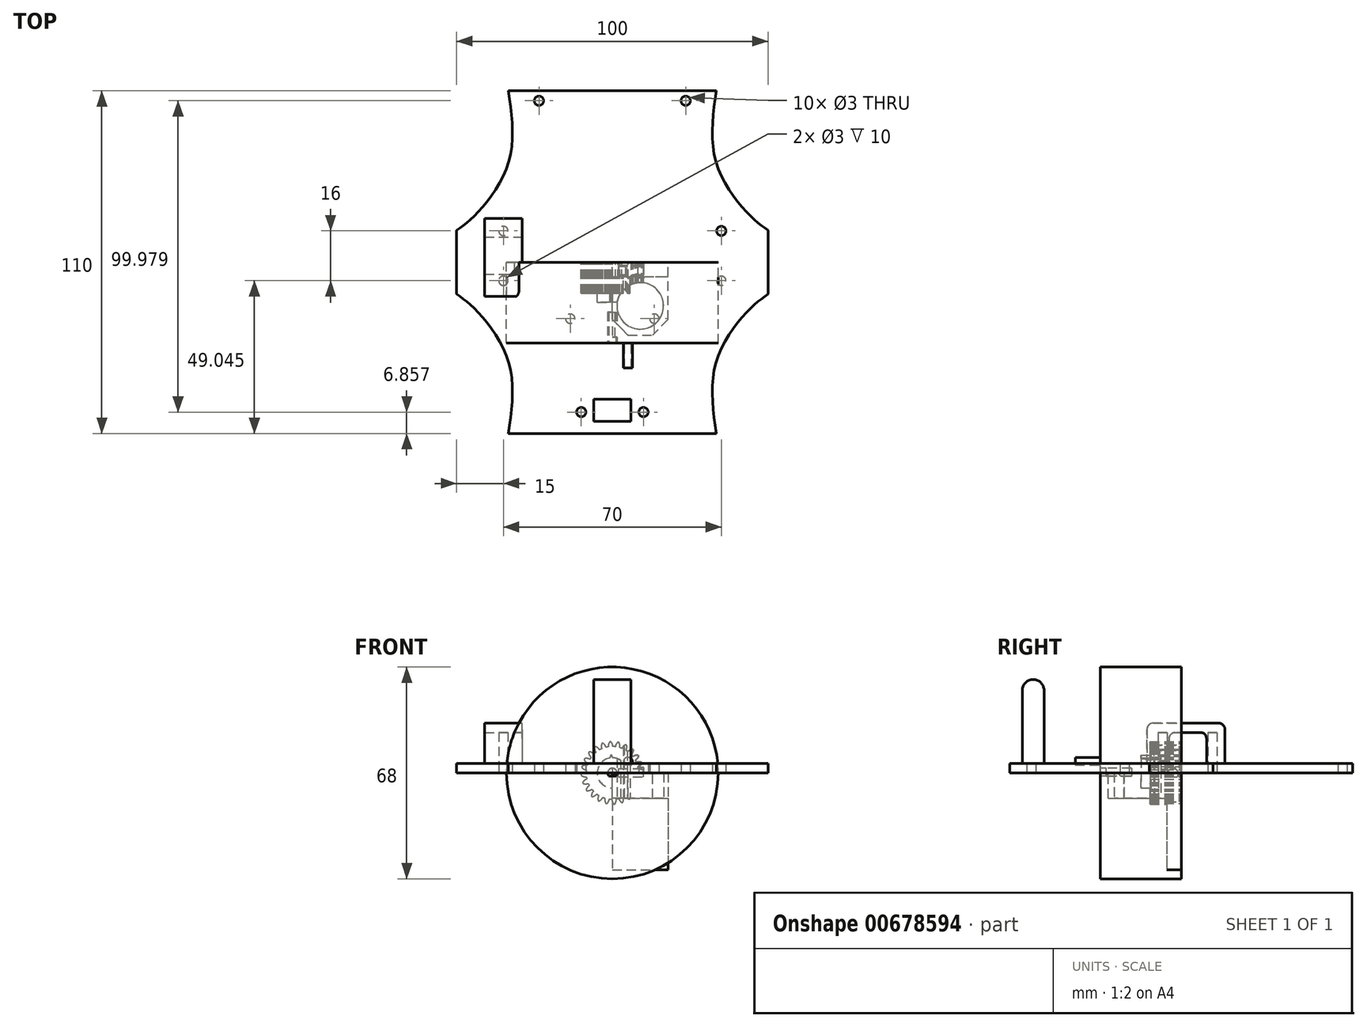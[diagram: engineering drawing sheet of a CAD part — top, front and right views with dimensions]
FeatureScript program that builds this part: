
annotation { "Feature Type Name" : "Feature", "Feature Type Description" : "" }
export const myFeature = defineFeature(function(context is Context, id is Id, definition is map)
    precondition{}
    {
        {
            var Q0;
            Q0=qCreatedBy(makeId("Front.planeOp"),FACE);
            var sketch = newSketch(context, id + "F0", { "sketchPlane" : qUnion([Q0])});
            skCircle(sketch, "E0", {"center": v(0, 0) * mm, "radius": 10 * mm, "construction": true});
            skCircle(sketch, "E1", {"center": v(0, 0) * mm, "radius": 9.24 * mm, "construction": true});
            skCircle(sketch, "E2", {"center": v(0, 0) * mm, "radius": 8.46 * mm});
            skLineSegment(sketch, "E3", {"start": v(0, 0) * mm, "end": v(0, 12.08) * mm, "construction": true});
            skLineSegment(sketch, "E4", {"start": v(0, 0) * mm, "end": v(-0.78, 11.94) * mm, "construction": true});
            skLineSegment(sketch, "E5", {"start": v(0, 9.24) * mm, "end": v(-6.89, 9.24) * mm, "construction": true});
            skLineSegment(sketch, "E6", {"start": v(0, 9.24) * mm, "end": v(-6.45, 6.9) * mm, "construction": true});
            skCircle(sketch, "E7", {"center": v(0, 9.24) * mm, "radius": 2.3 * mm, "construction": true});
            skCircle(sketch, "E8", {"center": v(0, 0) * mm, "radius": 8.68 * mm, "construction": true});
            skArc(sketch, "E9", {"start": v(0.15, 8.46) * mm, "mid": v(-0.02, 9.28) * mm, "end": v(-0.47, 9.99) * mm});
            skArc(sketch, "E10.MirrorCS", {"start": v(-1.26, 8.37) * mm, "mid": v(-1.2, 9.2) * mm, "end": v(-0.84, 9.97) * mm});
            skArc(sketch, "E11", {"start": v(-0.47, 9.99) * mm, "mid": v(-0.65, 9.99) * mm, "end": v(-0.84, 9.97) * mm});
            skArc(sketch, "E12.1.0", {"start": v(-2.04, 8.21) * mm, "mid": v(-2.42, 8.96) * mm, "end": v(-3.04, 9.53) * mm});
            skArc(sketch, "E12.1.1", {"start": v(-3.38, 7.76) * mm, "mid": v(-3.54, 8.58) * mm, "end": v(-3.39, 9.4) * mm});
            skArc(sketch, "E12.1.2", {"start": v(-3.04, 9.53) * mm, "mid": v(-3.22, 9.48) * mm, "end": v(-3.39, 9.4) * mm});
            skArc(sketch, "E12.2.0", {"start": v(-4.1, 7.4) * mm, "mid": v(-4.66, 8.03) * mm, "end": v(-5.4, 8.41) * mm});
            skArc(sketch, "E12.2.1", {"start": v(-5.27, 6.62) * mm, "mid": v(-5.64, 7.37) * mm, "end": v(-5.7, 8.21) * mm});
            skArc(sketch, "E12.2.2", {"start": v(-5.4, 8.41) * mm, "mid": v(-5.56, 8.32) * mm, "end": v(-5.7, 8.21) * mm});
            skArc(sketch, "E12.3.0", {"start": v(-5.87, 6.1) * mm, "mid": v(-6.58, 6.55) * mm, "end": v(-7.4, 6.73) * mm});
            skArc(sketch, "E12.3.1", {"start": v(-6.8, 5.03) * mm, "mid": v(-7.35, 5.66) * mm, "end": v(-7.64, 6.46) * mm});
            skArc(sketch, "E12.3.2", {"start": v(-7.4, 6.73) * mm, "mid": v(-7.53, 6.6) * mm, "end": v(-7.64, 6.46) * mm});
            skArc(sketch, "E12.4.0", {"start": v(-7.25, 4.36) * mm, "mid": v(-8.05, 4.63) * mm, "end": v(-8.89, 4.58) * mm});
            skArc(sketch, "E12.4.1", {"start": v(-7.87, 3.1) * mm, "mid": v(-8.57, 3.57) * mm, "end": v(-9.05, 4.26) * mm});
            skArc(sketch, "E12.4.2", {"start": v(-8.89, 4.58) * mm, "mid": v(-8.98, 4.43) * mm, "end": v(-9.05, 4.26) * mm});
            skArc(sketch, "E12.5.0", {"start": v(-8.13, 2.34) * mm, "mid": v(-8.97, 2.39) * mm, "end": v(-9.77, 2.13) * mm});
            skArc(sketch, "E12.5.1", {"start": v(-8.4, 0.95) * mm, "mid": v(-9.2, 1.23) * mm, "end": v(-9.84, 1.77) * mm});
            skArc(sketch, "E12.5.2", {"start": v(-9.77, 2.13) * mm, "mid": v(-9.82, 1.95) * mm, "end": v(-9.84, 1.77) * mm});
            skArc(sketch, "E12.6.0", {"start": v(-8.46, 0.15) * mm, "mid": v(-9.28, -0.02) * mm, "end": v(-9.99, -0.47) * mm});
            skArc(sketch, "E12.6.1", {"start": v(-8.37, -1.26) * mm, "mid": v(-9.2, -1.2) * mm, "end": v(-9.97, -0.84) * mm});
            skArc(sketch, "E12.6.2", {"start": v(-9.99, -0.47) * mm, "mid": v(-9.99, -0.65) * mm, "end": v(-9.97, -0.84) * mm});
            skArc(sketch, "E12.7.0", {"start": v(-8.21, -2.04) * mm, "mid": v(-8.96, -2.42) * mm, "end": v(-9.53, -3.04) * mm});
            skArc(sketch, "E12.7.1", {"start": v(-7.76, -3.38) * mm, "mid": v(-8.58, -3.54) * mm, "end": v(-9.4, -3.39) * mm});
            skArc(sketch, "E12.7.2", {"start": v(-9.53, -3.04) * mm, "mid": v(-9.48, -3.22) * mm, "end": v(-9.4, -3.39) * mm});
            skArc(sketch, "E12.8.0", {"start": v(-7.4, -4.1) * mm, "mid": v(-8.03, -4.66) * mm, "end": v(-8.41, -5.4) * mm});
            skArc(sketch, "E12.8.1", {"start": v(-6.62, -5.27) * mm, "mid": v(-7.37, -5.64) * mm, "end": v(-8.21, -5.7) * mm});
            skArc(sketch, "E12.8.2", {"start": v(-8.41, -5.4) * mm, "mid": v(-8.32, -5.56) * mm, "end": v(-8.21, -5.7) * mm});
            skArc(sketch, "E12.9.0", {"start": v(-6.1, -5.87) * mm, "mid": v(-6.55, -6.58) * mm, "end": v(-6.73, -7.4) * mm});
            skArc(sketch, "E12.9.1", {"start": v(-5.03, -6.8) * mm, "mid": v(-5.66, -7.35) * mm, "end": v(-6.46, -7.64) * mm});
            skArc(sketch, "E12.9.2", {"start": v(-6.73, -7.4) * mm, "mid": v(-6.6, -7.53) * mm, "end": v(-6.46, -7.64) * mm});
            skArc(sketch, "E12.10.0", {"start": v(-4.36, -7.25) * mm, "mid": v(-4.63, -8.05) * mm, "end": v(-4.58, -8.89) * mm});
            skArc(sketch, "E12.10.1", {"start": v(-3.1, -7.87) * mm, "mid": v(-3.57, -8.57) * mm, "end": v(-4.26, -9.05) * mm});
            skArc(sketch, "E12.10.2", {"start": v(-4.58, -8.89) * mm, "mid": v(-4.43, -8.98) * mm, "end": v(-4.26, -9.05) * mm});
            skArc(sketch, "E12.11.0", {"start": v(-2.34, -8.13) * mm, "mid": v(-2.39, -8.97) * mm, "end": v(-2.13, -9.77) * mm});
            skArc(sketch, "E12.11.1", {"start": v(-0.95, -8.4) * mm, "mid": v(-1.23, -9.2) * mm, "end": v(-1.77, -9.84) * mm});
            skArc(sketch, "E12.11.2", {"start": v(-2.13, -9.77) * mm, "mid": v(-1.95, -9.82) * mm, "end": v(-1.77, -9.84) * mm});
            skArc(sketch, "E12.12.0", {"start": v(-0.15, -8.46) * mm, "mid": v(0.02, -9.28) * mm, "end": v(0.47, -9.99) * mm});
            skArc(sketch, "E12.12.1", {"start": v(1.26, -8.37) * mm, "mid": v(1.2, -9.2) * mm, "end": v(0.84, -9.97) * mm});
            skArc(sketch, "E12.12.2", {"start": v(0.47, -9.99) * mm, "mid": v(0.65, -9.99) * mm, "end": v(0.84, -9.97) * mm});
            skArc(sketch, "E12.13.0", {"start": v(2.04, -8.21) * mm, "mid": v(2.42, -8.96) * mm, "end": v(3.04, -9.53) * mm});
            skArc(sketch, "E12.13.1", {"start": v(3.38, -7.76) * mm, "mid": v(3.54, -8.58) * mm, "end": v(3.39, -9.4) * mm});
            skArc(sketch, "E12.13.2", {"start": v(3.04, -9.53) * mm, "mid": v(3.22, -9.48) * mm, "end": v(3.39, -9.4) * mm});
            skArc(sketch, "E12.14.0", {"start": v(4.1, -7.4) * mm, "mid": v(4.66, -8.03) * mm, "end": v(5.4, -8.41) * mm});
            skArc(sketch, "E12.14.1", {"start": v(5.27, -6.62) * mm, "mid": v(5.64, -7.37) * mm, "end": v(5.7, -8.21) * mm});
            skArc(sketch, "E12.14.2", {"start": v(5.4, -8.41) * mm, "mid": v(5.56, -8.32) * mm, "end": v(5.7, -8.21) * mm});
            skArc(sketch, "E12.15.0", {"start": v(5.87, -6.1) * mm, "mid": v(6.58, -6.55) * mm, "end": v(7.4, -6.73) * mm});
            skArc(sketch, "E12.15.1", {"start": v(6.8, -5.03) * mm, "mid": v(7.35, -5.66) * mm, "end": v(7.64, -6.46) * mm});
            skArc(sketch, "E12.15.2", {"start": v(7.4, -6.73) * mm, "mid": v(7.53, -6.6) * mm, "end": v(7.64, -6.46) * mm});
            skArc(sketch, "E12.16.0", {"start": v(7.25, -4.36) * mm, "mid": v(8.05, -4.63) * mm, "end": v(8.89, -4.58) * mm});
            skArc(sketch, "E12.16.1", {"start": v(7.87, -3.1) * mm, "mid": v(8.57, -3.57) * mm, "end": v(9.05, -4.26) * mm});
            skArc(sketch, "E12.16.2", {"start": v(8.89, -4.58) * mm, "mid": v(8.98, -4.43) * mm, "end": v(9.05, -4.26) * mm});
            skArc(sketch, "E12.17.0", {"start": v(8.13, -2.34) * mm, "mid": v(8.97, -2.39) * mm, "end": v(9.77, -2.13) * mm});
            skArc(sketch, "E12.17.1", {"start": v(8.4, -0.95) * mm, "mid": v(9.2, -1.23) * mm, "end": v(9.84, -1.77) * mm});
            skArc(sketch, "E12.17.2", {"start": v(9.77, -2.13) * mm, "mid": v(9.82, -1.95) * mm, "end": v(9.84, -1.77) * mm});
            skArc(sketch, "E12.18.0", {"start": v(8.46, -0.15) * mm, "mid": v(9.28, 0.02) * mm, "end": v(9.99, 0.47) * mm});
            skArc(sketch, "E12.18.1", {"start": v(8.37, 1.26) * mm, "mid": v(9.2, 1.2) * mm, "end": v(9.97, 0.84) * mm});
            skArc(sketch, "E12.18.2", {"start": v(9.99, 0.47) * mm, "mid": v(9.99, 0.65) * mm, "end": v(9.97, 0.84) * mm});
            skArc(sketch, "E12.19.0", {"start": v(8.21, 2.04) * mm, "mid": v(8.96, 2.42) * mm, "end": v(9.53, 3.04) * mm});
            skArc(sketch, "E12.19.1", {"start": v(7.76, 3.38) * mm, "mid": v(8.58, 3.54) * mm, "end": v(9.4, 3.39) * mm});
            skArc(sketch, "E12.19.2", {"start": v(9.53, 3.04) * mm, "mid": v(9.48, 3.22) * mm, "end": v(9.4, 3.39) * mm});
            skArc(sketch, "E12.20.0", {"start": v(7.4, 4.1) * mm, "mid": v(8.03, 4.66) * mm, "end": v(8.41, 5.4) * mm});
            skArc(sketch, "E12.20.1", {"start": v(6.62, 5.27) * mm, "mid": v(7.37, 5.64) * mm, "end": v(8.21, 5.7) * mm});
            skArc(sketch, "E12.20.2", {"start": v(8.41, 5.4) * mm, "mid": v(8.32, 5.56) * mm, "end": v(8.21, 5.7) * mm});
            skArc(sketch, "E12.21.0", {"start": v(6.1, 5.87) * mm, "mid": v(6.55, 6.58) * mm, "end": v(6.73, 7.4) * mm});
            skArc(sketch, "E12.21.1", {"start": v(5.03, 6.8) * mm, "mid": v(5.66, 7.35) * mm, "end": v(6.46, 7.64) * mm});
            skArc(sketch, "E12.21.2", {"start": v(6.73, 7.4) * mm, "mid": v(6.6, 7.53) * mm, "end": v(6.46, 7.64) * mm});
            skArc(sketch, "E12.22.0", {"start": v(4.36, 7.25) * mm, "mid": v(4.63, 8.05) * mm, "end": v(4.58, 8.89) * mm});
            skArc(sketch, "E12.22.1", {"start": v(3.1, 7.87) * mm, "mid": v(3.57, 8.57) * mm, "end": v(4.26, 9.05) * mm});
            skArc(sketch, "E12.22.2", {"start": v(4.58, 8.89) * mm, "mid": v(4.43, 8.98) * mm, "end": v(4.26, 9.05) * mm});
            skArc(sketch, "E12.23.0", {"start": v(2.34, 8.13) * mm, "mid": v(2.39, 8.97) * mm, "end": v(2.13, 9.77) * mm});
            skArc(sketch, "E12.23.1", {"start": v(0.95, 8.4) * mm, "mid": v(1.23, 9.2) * mm, "end": v(1.77, 9.84) * mm});
            skArc(sketch, "E12.23.2", {"start": v(2.13, 9.77) * mm, "mid": v(1.95, 9.82) * mm, "end": v(1.77, 9.84) * mm});
            skCircle(sketch, "E13", {"center": v(-3.42, 7.98) * mm, "radius": 3.64 * mm, "construction": true});
            skSolve(sketch);
        }
        {
            var Q0;
            Q0=qSketchRegion(id+"F0",true);
            extrude(context, id + "F1", {"entities" : qUnion([Q0]), "depth" : 10 * mm});
        }
        {
            var Q0;
            Q0=qCreatedBy(makeId("Front.planeOp"),FACE);
            var sketch = newSketch(context, id + "F2", { "sketchPlane" : qUnion([Q0])});
            skCircle(sketch, "E14", {"center": v(0, 0) * mm, "radius": 2.31 * mm, "construction": true});
            skCircle(sketch, "E15", {"center": v(0, 0) * mm, "radius": 2.12 * mm});
            skCircle(sketch, "E16", {"center": v(0, 0) * mm, "radius": 2.5 * mm, "construction": true});
            skLineSegment(sketch, "E17", {"start": v(0, 0) * mm, "end": v(0, 3.7) * mm, "construction": true});
            skLineSegment(sketch, "E18", {"start": v(0, 0) * mm, "end": v(-0.23, 3.58) * mm, "construction": true});
            skLineSegment(sketch, "E19", {"start": v(0, 2.31) * mm, "end": v(-2.42, 1.43) * mm, "construction": true});
            skLineSegment(sketch, "E20", {"start": v(0, 2.3) * mm, "end": v(-1.97, 2.3) * mm, "construction": true});
            skCircle(sketch, "E21", {"center": v(0, 0) * mm, "radius": 2.17 * mm, "construction": true});
            skCircle(sketch, "E22", {"center": v(-0.54, 2.1) * mm, "radius": 0.57 * mm, "construction": true});
            skArc(sketch, "E23", {"start": v(0.04, 2.11) * mm, "mid": v(0.03, 2.21) * mm, "end": v(0, 2.31) * mm});
            skArc(sketch, "E24", {"start": v(0, 2.3) * mm, "mid": v(-0.05, 2.4) * mm, "end": v(-0.12, 2.5) * mm});
            skArc(sketch, "E25.MirrorCS", {"start": v(-0.3, 2.3) * mm, "mid": v(-0.27, 2.4) * mm, "end": v(-0.21, 2.5) * mm});
            skArc(sketch, "E26.MirrorCS", {"start": v(-0.32, 2.1) * mm, "mid": v(-0.32, 2.2) * mm, "end": v(-0.3, 2.3) * mm});
            skArc(sketch, "E27", {"start": v(-0.12, 2.5) * mm, "mid": v(-0.16, 2.5) * mm, "end": v(-0.21, 2.5) * mm});
            skArc(sketch, "E28.1.0", {"start": v(-1.83, -1.4) * mm, "mid": v(-1.94, -1.43) * mm, "end": v(-2.05, -1.43) * mm});
            skArc(sketch, "E28.1.1", {"start": v(-1.65, -1.32) * mm, "mid": v(-1.74, -1.37) * mm, "end": v(-1.83, -1.4) * mm});
            skArc(sketch, "E28.1.2", {"start": v(-2.1, -1.35) * mm, "mid": v(-2.08, -1.4) * mm, "end": v(-2.05, -1.43) * mm});
            skArc(sketch, "E28.2.0", {"start": v(2.13, -0.88) * mm, "mid": v(2.2, -0.97) * mm, "end": v(2.26, -1.06) * mm});
            skArc(sketch, "E28.2.1", {"start": v(1.97, -0.77) * mm, "mid": v(2.06, -0.82) * mm, "end": v(2.13, -0.88) * mm});
            skArc(sketch, "E28.2.2", {"start": v(2.22, -1.15) * mm, "mid": v(2.25, -1.1) * mm, "end": v(2.26, -1.06) * mm});
            skCircle(sketch, "E29", {"center": v(0, 2.31) * mm, "radius": 0.57 * mm, "construction": true});
            skSolve(sketch);
        }
        {
            var Q0;
            Q0=qSketchRegion(id+"F2",true);
            extrude(context, id + "F3", {"entities" : qUnion([Q0]), "depth" : 5.62 * mm});
        }
        {
            var Q0;
            Q0=makeQuery(id+"F3.opExtrude","SWEPT_BODY",BODY,{"disambiguationData":[OSD([sQuery(id+"F2.wireOp",EDGE,"E15"),sQuery(id+"F2.wireOp",EDGE,"E23"),sQuery(id+"F2.wireOp",EDGE,"E24"),sQuery(id+"F2.wireOp",EDGE,"E25.MirrorCS"),sQuery(id+"F2.wireOp",EDGE,"E26.MirrorCS"),sQuery(id+"F2.wireOp",EDGE,"E27")])]});
            var Q1;
            Q1=qCreatedBy(makeId("Origin.pointOp"),VERTEX);
            transform(context, id + "F4", {"entities" : qUnion([Q0]), "transformType" : TransformType.SCALE_UNIFORMLY, "scale" : 2.3, "scalePoint" : qUnion([Q1]), "makeCopy" : false});
        }
        {
            var Q0;
            Q0=qCreatedBy(makeId("Front.planeOp"),FACE);
            var sketch = newSketch(context, id + "F5", { "sketchPlane" : qUnion([Q0])});
            skLineSegment(sketch, "E30.bottom", {"start": v(0, 0) * mm, "end": v(17.91, 0) * mm});
            skLineSegment(sketch, "E30.top", {"start": v(0, -31.13) * mm, "end": v(17.91, -31.13) * mm});
            skLineSegment(sketch, "E30.left", {"start": v(0, 0) * mm, "end": v(0, -31.13) * mm});
            skLineSegment(sketch, "E30.right", {"start": v(17.91, 0) * mm, "end": v(17.91, -31.13) * mm});
            skSolve(sketch);
        }
        {
            var Q0;
            Q0=qSketchRegion(id+"F5",true);
            extrude(context, id + "F6", {"entities" : qUnion([Q0]), "depth" : 4.6 * mm, "offsetDistance" : 25 * mm});
        }
        {
            var Q0;
            Q0=makeQuery(id+"F6.opExtrude","CAP_FACE",FACE,{"disambiguationData":[OSD([sQuery(id+"F5.wireOp",EDGE,"E30.bottom"),sQuery(id+"F5.wireOp",EDGE,"E30.top"),sQuery(id+"F5.wireOp",EDGE,"E30.left"),sQuery(id+"F5.wireOp",EDGE,"E30.right")])],"isStart":false});
            var sketch = newSketch(context, id + "F7", { "sketchPlane" : qUnion([Q0])});
            skLineSegment(sketch, "E31.bottom", {"start": v(0, 0) * mm, "end": v(17.91, 0) * mm});
            skLineSegment(sketch, "E31.top", {"start": v(0, -8.15) * mm, "end": v(17.91, -8.15) * mm});
            skLineSegment(sketch, "E31.left", {"start": v(0, 0) * mm, "end": v(0, -8.15) * mm});
            skLineSegment(sketch, "E31.right", {"start": v(17.91, 0) * mm, "end": v(17.91, -8.15) * mm});
            skSolve(sketch);
        }
        {
            var Q0;
            Q0=qSketchRegion(id+"F7",true);
            extrude(context, id + "F8", {"entities" : qUnion([Q0]), "operationType" : NewBodyOperationType.ADD, "depth" : 18.8 * mm, "offsetDistance" : 25 * mm});
        }
        {
            var Q0;
            Q0=makeQuery(id+"F8.opExtrude","SWEPT_FACE",FACE,{"disambiguationData":[OSD([sQuery(id+"F7.wireOp",EDGE,"E31.top")])]});
            var sketch = newSketch(context, id + "F9", { "sketchPlane" : qUnion([Q0])});
            skLineSegment(sketch, "E32", {"start": v(0, 23.4) * mm, "end": v(17.91, 4.6) * mm});
            skLineSegment(sketch, "E33", {"start": v(17.91, 4.6) * mm, "end": v(17.91, 23.4) * mm});
            skLineSegment(sketch, "E34", {"start": v(17.91, 23.4) * mm, "end": v(0, 4.6) * mm});
            skCircle(sketch, "E35", {"center": v(8.96, 14) * mm, "radius": 7.48 * mm});
            skSolve(sketch);
        }
        {
            var Q0;
            {var subQ0=sQuery(id+"F9.wireOp",EDGE,"E35");var subQ1=sQuery(id+"F9.wireOp",EDGE,"E32");var subQ2=makeQuery(id+"F9.imprint","INTERSECT",VERTEX,{"disambiguationData":[OD(0.0)],"derivedFrom":[subQ1,subQ0]});Q0=makeQuery(id+"F9.imprint","IMPRINT",FACE,{"disambiguationData":[TD([[makeQuery(id+"F9.imprint","IMPRINT",EDGE,{"disambiguationData":[TD([[subQ2,-1.0]])],"derivedFrom":subQ1}),-1.0]])]});}
            var Q1;
            {var subQ0=sQuery(id+"F9.wireOp",EDGE,"E35");var subQ1=sQuery(id+"F9.wireOp",EDGE,"E32");var subQ2=makeQuery(id+"F9.imprint","INTERSECT",VERTEX,{"disambiguationData":[OD(0.0)],"derivedFrom":[subQ1,subQ0]});Q1=makeQuery(id+"F9.imprint","IMPRINT",FACE,{"disambiguationData":[TD([[makeQuery(id+"F9.imprint","IMPRINT",EDGE,{"disambiguationData":[TD([[subQ2,-1.0]])],"derivedFrom":subQ1}),1.0]])]});}
            var Q2;
            {var subQ0=sQuery(id+"F9.wireOp",EDGE,"E34");var subQ1=sQuery(id+"F9.wireOp",EDGE,"E32");var subQ2=makeQuery(id+"F9.imprint","INTERSECT",VERTEX,{"derivedFrom":[subQ1,subQ0]});Q2=makeQuery(id+"F9.imprint","IMPRINT",FACE,{"disambiguationData":[TD([[makeQuery(id+"F9.imprint","IMPRINT",EDGE,{"disambiguationData":[TD([[subQ2,-1.0]])],"derivedFrom":subQ1}),1.0]])]});}
            var Q3;
            {var subQ0=sQuery(id+"F9.wireOp",EDGE,"E34");var subQ1=sQuery(id+"F9.wireOp",EDGE,"E32");var subQ2=makeQuery(id+"F9.imprint","INTERSECT",VERTEX,{"derivedFrom":[subQ1,subQ0]});Q3=makeQuery(id+"F9.imprint","IMPRINT",FACE,{"disambiguationData":[TD([[makeQuery(id+"F9.imprint","IMPRINT",EDGE,{"disambiguationData":[TD([[subQ2,-1.0]])],"derivedFrom":subQ1}),-1.0]])]});}
            extrude(context, id + "F10", {"entities" : qUnion([Q0, Q1, Q2, Q3]), "operationType" : NewBodyOperationType.REMOVE, "oppositeDirection" : true, "depth" : 25 * mm, "offsetDistance" : 25 * mm});
        }
        {
            var Q0;
            Q0=makeQuery(id+"F8.opExtrude","CAP_EDGE",EDGE,{"disambiguationData":[OSD([sQuery(id+"F7.wireOp",EDGE,"E31.left")])],"isStart":false});
            var Q1;
            Q1=makeQuery(id+"F8.opExtrude","CAP_EDGE",EDGE,{"disambiguationData":[OSD([sQuery(id+"F7.wireOp",EDGE,"E31.right")])],"isStart":false});
            chamfer(context, id + "F11", {"entities" : qUnion([Q0, Q1]), "width" : 5 * mm, "tangentPropagation" : true});
        }
        {
            var Q0;
            Q0=qCreatedBy(makeId("Right.planeOp"),FACE);
            var sketch = newSketch(context, id + "F12", { "sketchPlane" : qUnion([Q0])});
            skLineSegment(sketch, "E36", {"start": v(0, 0) * mm, "end": v(-5.3, 0) * mm});
            skLineSegment(sketch, "E37", {"start": v(-2.65, 0) * mm, "end": v(-2.65, 1.75) * mm});
            skLineSegment(sketch, "E38", {"start": v(-2.65, 1.75) * mm, "end": v(-2.65, -1.75) * mm});
            skLineSegment(sketch, "E39", {"start": v(2.53, 1.75) * mm, "end": v(-9.07, 1.75) * mm});
            skLineSegment(sketch, "E40", {"start": v(-9.07, -1.75) * mm, "end": v(4.89, -1.75) * mm});
            skArc(sketch, "E41", {"start": v(-0.53, -1.75) * mm, "mid": v(0, 0) * mm, "end": v(-0.53, 1.75) * mm});
            skArc(sketch, "E42.MirrorCS", {"start": v(-4.77, -1.75) * mm, "mid": v(-5.3, 0) * mm, "end": v(-4.77, 1.75) * mm});
            skSolve(sketch);
        }
        {
            var Q0;
            {var subQ0=sQuery(id+"F12.wireOp",EDGE,"E41");var subQ1=sQuery(id+"F12.wireOp",EDGE,"E36");var subQ2=makeQuery(id+"F12.imprint","INTERSECT",VERTEX,{"derivedFrom":[subQ1,subQ0]});Q0=makeQuery(id+"F12.imprint","IMPRINT",FACE,{"disambiguationData":[TD([[makeQuery(id+"F12.imprint","IMPRINT",EDGE,{"disambiguationData":[TD([[subQ2,-1.0]])],"derivedFrom":subQ1}),-1.0]])]});}
            var Q1;
            {var subQ0=sQuery(id+"F12.wireOp",EDGE,"E42.MirrorCS");var subQ1=sQuery(id+"F12.wireOp",EDGE,"E36");var subQ2=makeQuery(id+"F12.imprint","INTERSECT",VERTEX,{"derivedFrom":[subQ1,subQ0]});Q1=makeQuery(id+"F12.imprint","IMPRINT",FACE,{"disambiguationData":[TD([[makeQuery(id+"F12.imprint","IMPRINT",EDGE,{"disambiguationData":[TD([[subQ2,1.0]])],"derivedFrom":subQ1}),-1.0]])]});}
            var Q2;
            {var subQ0=sQuery(id+"F12.wireOp",EDGE,"E42.MirrorCS");var subQ1=sQuery(id+"F12.wireOp",EDGE,"E36");var subQ2=makeQuery(id+"F12.imprint","INTERSECT",VERTEX,{"derivedFrom":[subQ1,subQ0]});Q2=makeQuery(id+"F12.imprint","IMPRINT",FACE,{"disambiguationData":[TD([[makeQuery(id+"F12.imprint","IMPRINT",EDGE,{"disambiguationData":[TD([[subQ2,1.0]])],"derivedFrom":subQ1}),1.0]])]});}
            var Q3;
            {var subQ0=sQuery(id+"F12.wireOp",EDGE,"E41");var subQ1=sQuery(id+"F12.wireOp",EDGE,"E36");var subQ2=makeQuery(id+"F12.imprint","INTERSECT",VERTEX,{"derivedFrom":[subQ1,subQ0]});Q3=makeQuery(id+"F12.imprint","IMPRINT",FACE,{"disambiguationData":[TD([[makeQuery(id+"F12.imprint","IMPRINT",EDGE,{"disambiguationData":[TD([[subQ2,-1.0]])],"derivedFrom":subQ1}),1.0]])]});}
            extrude(context, id + "F13", {"entities" : qUnion([Q0, Q1, Q2, Q3]), "depth" : 10 * mm, "offsetDistance" : 25 * mm});
        }
        {
            var Q0;
            Q0=makeQuery(id+"F13.opExtrude","CAP_FACE",FACE,{"disambiguationData":[OSD([sQuery(id+"F12.wireOp",EDGE,"E39"),sQuery(id+"F12.wireOp",EDGE,"E40"),sQuery(id+"F12.wireOp",EDGE,"E41"),sQuery(id+"F12.wireOp",EDGE,"E42.MirrorCS")])],"isStart":false});
            var sketch = newSketch(context, id + "F14", { "sketchPlane" : qUnion([Q0])});
            skLineSegment(sketch, "E43", {"start": v(-0.53, -1.75) * mm, "end": v(-0.53, 1.75) * mm});
            skArc(sketch, "E44", {"start": v(-1.27, -1.28) * mm, "mid": v(-2.65, 1.42) * mm, "end": v(-4.03, -1.28) * mm});
            skLineSegment(sketch, "E45", {"start": v(-2.65, -1.28) * mm, "end": v(-1.27, -1.28) * mm});
            skLineSegment(sketch, "E46", {"start": v(-1.27, -1.28) * mm, "end": v(-4.03, -1.28) * mm});
            skLineSegment(sketch, "E47", {"start": v(0, 0) * mm, "end": v(0, -5.33) * mm});
            skLineSegment(sketch, "E48", {"start": v(-3.2, -5.33) * mm, "end": v(0, -5.33) * mm});
            skSolve(sketch);
        }
        {
            var Q0;
            {var subQ0=sQuery(id+"F14.wireOp",EDGE,"E44");Q0=makeQuery(id+"F14.imprint","IMPRINT",FACE,{"disambiguationData":[TD([[makeQuery(id+"F14.imprint","IMPRINT",EDGE,{"derivedFrom":subQ0}),1.0]])]});}
            extrude(context, id + "F15", {"entities" : qUnion([Q0]), "operationType" : NewBodyOperationType.REMOVE, "oppositeDirection" : true, "depth" : 8 * mm, "offsetDistance" : 25 * mm});
        }
        {
            var Q0;
            Q0=makeQuery(id+"F13.opExtrude","CAP_FACE",FACE,{"disambiguationData":[OSD([sQuery(id+"F12.wireOp",EDGE,"E39"),sQuery(id+"F12.wireOp",EDGE,"E40"),sQuery(id+"F12.wireOp",EDGE,"E41"),sQuery(id+"F12.wireOp",EDGE,"E42.MirrorCS")])],"isStart":true});
            extrude(context, id + "F16", {"entities" : qUnion([Q0]), "operationType" : NewBodyOperationType.ADD, "depth" : 3 * mm, "offsetDistance" : 25 * mm});
        }
        {
            var Q0;
            Q0=qCreatedBy(makeId("Front.planeOp"),FACE);
            var sketch = newSketch(context, id + "F17", { "sketchPlane" : qUnion([Q0])});
            skCircle(sketch, "E49", {"center": v(0, 0) * mm, "radius": 34 * mm});
            skSolve(sketch);
        }
        {
            var Q0;
            Q0=qSketchRegion(id+"F17",true);
            extrude(context, id + "F18", {"entities" : qUnion([Q0]), "depth" : 26 * mm, "offsetDistance" : 25 * mm});
        }
        {
            var Q0;
            Q0=makeQuery(id+"F18.opExtrude","CAP_FACE",FACE,{"disambiguationData":[OSD([sQuery(id+"F17.wireOp",EDGE,"E49")])],"isStart":false});
            var sketch = newSketch(context, id + "F19", { "sketchPlane" : qUnion([Q0])});
            skArc(sketch, "E50", {"start": v(1.12, -1) * mm, "mid": v(0, 1.5) * mm, "end": v(-1.12, -1) * mm});
            skLineSegment(sketch, "E51", {"start": v(0, 1.5) * mm, "end": v(0, -1) * mm});
            skLineSegment(sketch, "E52", {"start": v(-1.12, -1) * mm, "end": v(1.12, -1) * mm});
            skSolve(sketch);
        }
        {
            var Q0;
            Q0=qSketchRegion(id+"F19",true);
            extrude(context, id + "F20", {"entities" : qUnion([Q0]), "operationType" : NewBodyOperationType.REMOVE, "oppositeDirection" : true, "depth" : 10 * mm, "offsetDistance" : 25 * mm});
        }
        {
            var Q0;
            Q0=qCreatedBy(makeId("Front.planeOp"),FACE);
            var sketch = newSketch(context, id + "F21", { "sketchPlane" : qUnion([Q0])});
            skLineSegment(sketch, "E53", {"start": v(0, 0) * mm, "end": v(0, 7) * mm});
            skLineSegment(sketch, "E54", {"start": v(10, 7) * mm, "end": v(10, 0) * mm});
            skArc(sketch, "E55", {"start": v(10, 7) * mm, "mid": v(5, 9.6) * mm, "end": v(0, 7) * mm});
            skArc(sketch, "E56", {"start": v(0, 0) * mm, "mid": v(5, -2.6) * mm, "end": v(10, 0) * mm});
            skLineSegment(sketch, "E57", {"start": v(0, 7) * mm, "end": v(10, 0) * mm});
            skLineSegment(sketch, "E58", {"start": v(0, 0) * mm, "end": v(10, 7) * mm});
            skSolve(sketch);
        }
        {
            var Q0;
            Q0=qSketchRegion(id+"F21",true);
            extrude(context, id + "F22", {"entities" : qUnion([Q0]), "depth" : 24 * mm, "offsetDistance" : 25 * mm});
        }
        {
            var Q0;
            Q0=makeQuery(id+"F22.opExtrude","CAP_FACE",FACE,{"disambiguationData":[OSD([sQuery(id+"F21.wireOp",EDGE,"E53"),sQuery(id+"F21.wireOp",EDGE,"E54"),sQuery(id+"F21.wireOp",EDGE,"E55"),sQuery(id+"F21.wireOp",EDGE,"E56")])],"isStart":false});
            var sketch = newSketch(context, id + "F23", { "sketchPlane" : qUnion([Q0])});
            skArc(sketch, "E59", {"start": v(6.12, 2.5) * mm, "mid": v(5, 5) * mm, "end": v(3.88, 2.5) * mm});
            skLineSegment(sketch, "E60", {"start": v(5, 2.5) * mm, "end": v(6.12, 2.5) * mm});
            skLineSegment(sketch, "E61", {"start": v(6.12, 2.5) * mm, "end": v(3.88, 2.5) * mm});
            skSolve(sketch);
        }
        {
            var Q0;
            Q0=qSketchRegion(id+"F23",true);
            extrude(context, id + "F24", {"entities" : qUnion([Q0]), "operationType" : NewBodyOperationType.ADD, "depth" : 10 * mm, "offsetDistance" : 25 * mm});
        }
        {
            var Q0;
            Q0=qCreatedBy(makeId("Top.planeOp"),FACE);
            var sketch = newSketch(context, id + "F25", { "sketchPlane" : qUnion([Q0])});
            skLineSegment(sketch, "E62.bottom", {"start": v(33.36, 55) * mm, "end": v(-33.36, 55) * mm});
            skLineSegment(sketch, "E62.top", {"start": v(33.36, -55) * mm, "end": v(-33.36, -55) * mm});
            skLineSegment(sketch, "E62.left", {"start": v(50, 10.27) * mm, "end": v(50, -10.27) * mm});
            skLineSegment(sketch, "E62.right", {"start": v(-50, 10.27) * mm, "end": v(-50, -10.27) * mm});
            skPoint(sketch, "E62.middle", {"position": v(0, 0) * mm});
            skCircle(sketch, "E63", {"center": v(-13.5, -18.14) * mm, "radius": 1.5 * mm});
            skCircle(sketch, "E64", {"center": v(13.5, -18.14) * mm, "radius": 1.5 * mm});
            skLineSegment(sketch, "E65.bottom", {"start": v(-26.5, 4.36) * mm, "end": v(26.5, 4.36) * mm});
            skLineSegment(sketch, "E65.top", {"start": v(-26.5, -53.14) * mm, "end": v(26.5, -53.14) * mm});
            skLineSegment(sketch, "E65.left", {"start": v(-26.5, 4.36) * mm, "end": v(-26.5, -53.14) * mm});
            skLineSegment(sketch, "E65.right", {"start": v(26.5, 4.36) * mm, "end": v(26.5, -53.14) * mm});
            skLineSegment(sketch, "E66.bottom", {"start": v(26.5, -53.14) * mm, "end": v(-26.5, -53.14) * mm});
            skLineSegment(sketch, "E66.top", {"start": v(26.5, 14.86) * mm, "end": v(-26.5, 14.86) * mm});
            skLineSegment(sketch, "E66.left", {"start": v(26.5, -53.14) * mm, "end": v(26.5, 14.86) * mm});
            skLineSegment(sketch, "E66.right", {"start": v(-26.5, -53.14) * mm, "end": v(-26.5, 14.86) * mm});
            skPoint(sketch, "E66.middle", {"position": v(0, -19.14) * mm});
            skCircle(sketch, "E67", {"center": v(35, 10.04) * mm, "radius": 1.5 * mm});
            skCircle(sketch, "E68", {"center": v(35, -5.96) * mm, "radius": 1.5 * mm});
            skCircle(sketch, "E69.MirrorC", {"center": v(-35, 10.04) * mm, "radius": 1.5 * mm});
            skCircle(sketch, "E70.MirrorC", {"center": v(-35, -5.96) * mm, "radius": 1.5 * mm});
            skFitSpline(sketch, "E71", {"points": [v(-33.36, -55) * mm, v(-33.36, -31.94) * mm, v(-43.92, -15.27) * mm, v(-50, -10.27) * mm], "startDerivative": vector(8.25, 59.38) * mm, "endDerivative": vector(-24.16, 17.14) * mm});
            skFitSpline(sketch, "E72.MirrorCS", {"points": [v(-33.36, 55) * mm, v(-33.36, 31.94) * mm, v(-43.92, 15.27) * mm, v(-50, 10.27) * mm], "startDerivative": vector(8.25, -59.38) * mm, "endDerivative": vector(-24.16, -17.14) * mm});
            skFitSpline(sketch, "E73.MirrorCS", {"points": [v(33.36, 55) * mm, v(33.36, 31.94) * mm, v(43.92, 15.27) * mm, v(50, 10.27) * mm], "startDerivative": vector(-8.25, -59.38) * mm, "endDerivative": vector(24.16, -17.14) * mm});
            skFitSpline(sketch, "E74.MirrorCS", {"points": [v(33.36, -55) * mm, v(33.36, -31.94) * mm, v(43.92, -15.27) * mm, v(50, -10.27) * mm], "startDerivative": vector(-8.25, 59.38) * mm, "endDerivative": vector(24.16, 17.14) * mm});
            skPoint(sketch, "E75.orphan", {"position": v(50, 55) * mm});
            skPoint(sketch, "E76.orphan", {"position": v(50, -55) * mm});
            skPoint(sketch, "E77.orphan", {"position": v(-50, -55) * mm});
            skPoint(sketch, "E78.orphan", {"position": v(-50, 55) * mm});
            skCircle(sketch, "E79", {"center": v(-23.56, 51.84) * mm, "radius": 1.5 * mm});
            skCircle(sketch, "E80.MirrorC", {"center": v(23.56, 51.84) * mm, "radius": 1.5 * mm});
            skCircle(sketch, "E81", {"center": v(10, -48.14) * mm, "radius": 1.5 * mm});
            skCircle(sketch, "E82", {"center": v(-10, -48.14) * mm, "radius": 1.5 * mm});
            skSolve(sketch);
        }
        {
            var Q0;
            Q0=makeQuery(id+"F25.imprint","IMPRINT",FACE,{"disambiguationData":[TD([[makeQuery(id+"F25.imprint","IMPRINT",EDGE,{"derivedFrom":sQuery(id+"F25.wireOp",EDGE,"E62.bottom")}),1.0]])]});
            var Q1;
            Q1=makeQuery(id+"F25.imprint","IMPRINT",FACE,{"disambiguationData":[TD([[makeQuery(id+"F25.imprint","IMPRINT",EDGE,{"derivedFrom":sQuery(id+"F25.wireOp",EDGE,"E63")}),-1.0]])]});
            var Q2;
            {var subQ0=sQuery(id+"F25.wireOp",EDGE,"E65.bottom");Q2=makeQuery(id+"F25.imprint","IMPRINT",FACE,{"disambiguationData":[TD([[makeQuery(id+"F25.imprint","IMPRINT",EDGE,{"derivedFrom":subQ0}),1.0]])]});}
            extrude(context, id + "F26", {"entities" : qUnion([Q0, Q1, Q2]), "depth" : 3 * mm, "offsetDistance" : 25 * mm});
        }
        {
            var Q0;
            Q0=makeQuery(id+"F26.opExtrude","CAP_FACE",FACE,{"disambiguationData":[OSD([sQuery(id+"F25.wireOp",EDGE,"E62.bottom"),sQuery(id+"F25.wireOp",EDGE,"E62.top"),sQuery(id+"F25.wireOp",EDGE,"E62.left"),sQuery(id+"F25.wireOp",EDGE,"E62.right"),sQuery(id+"F25.wireOp",EDGE,"E63"),sQuery(id+"F25.wireOp",EDGE,"E64"),sQuery(id+"F25.wireOp",EDGE,"E67"),sQuery(id+"F25.wireOp",EDGE,"E68"),sQuery(id+"F25.wireOp",EDGE,"E69.MirrorC"),sQuery(id+"F25.wireOp",EDGE,"E70.MirrorC"),sQuery(id+"F25.wireOp",EDGE,"E71"),sQuery(id+"F25.wireOp",EDGE,"E72.MirrorCS"),sQuery(id+"F25.wireOp",EDGE,"E73.MirrorCS"),sQuery(id+"F25.wireOp",EDGE,"E74.MirrorCS"),sQuery(id+"F25.wireOp",EDGE,"E79"),sQuery(id+"F25.wireOp",EDGE,"E80.MirrorC")])],"isStart":false});
            var sketch = newSketch(context, id + "F27", { "sketchPlane" : qUnion([Q0])});
            skLineSegment(sketch, "E83.bottom", {"start": v(-41, 14.03) * mm, "end": v(-29, 14.03) * mm});
            skLineSegment(sketch, "E83.top", {"start": v(-41, -10.97) * mm, "end": v(-29, -10.97) * mm});
            skLineSegment(sketch, "E83.left", {"start": v(-41, 14.03) * mm, "end": v(-41, -10.97) * mm});
            skLineSegment(sketch, "E83.right", {"start": v(-29, 14.03) * mm, "end": v(-29, -10.97) * mm});
            skCircle(sketch, "E84", {"center": v(-35, 10.04) * mm, "radius": 1.5 * mm});
            skCircle(sketch, "E85", {"center": v(-35, -5.96) * mm, "radius": 1.5 * mm});
            skLineSegment(sketch, "E86.bottom", {"start": v(-41, 8.13) * mm, "end": v(-29, 8.13) * mm});
            skLineSegment(sketch, "E86.top", {"start": v(-41, -3.87) * mm, "end": v(-29, -3.87) * mm});
            skLineSegment(sketch, "E86.left", {"start": v(-41, 8.13) * mm, "end": v(-41, -3.87) * mm});
            skLineSegment(sketch, "E86.right", {"start": v(-29, 8.13) * mm, "end": v(-29, -3.87) * mm});
            skSolve(sketch);
        }
        {
            var Q0;
            {var subQ1=sQuery(id+"F27.wireOp",EDGE,"E83.bottom");Q0=makeQuery(id+"F27.imprint","IMPRINT",FACE,{"disambiguationData":[TD([[makeQuery(id+"F27.imprint","IMPRINT",EDGE,{"derivedFrom":subQ1}),-1.0]])]});}
            var Q1;
            {var subQ1=sQuery(id+"F27.wireOp",EDGE,"E83.top");Q1=makeQuery(id+"F27.imprint","IMPRINT",FACE,{"disambiguationData":[TD([[makeQuery(id+"F27.imprint","IMPRINT",EDGE,{"derivedFrom":subQ1}),1.0]])]});}
            extrude(context, id + "F28", {"entities" : qUnion([Q0, Q1]), "depth" : 10 * mm, "offsetDistance" : 25 * mm});
        }
        {
            var Q0;
            Q0=makeQuery(id+"F28.opExtrude","CAP_FACE",FACE,{"disambiguationData":[OSD([sQuery(id+"F27.wireOp",EDGE,"E83.bottom"),sQuery(id+"F27.wireOp",EDGE,"E83.left"),sQuery(id+"F27.wireOp",EDGE,"E83.right"),sQuery(id+"F27.wireOp",EDGE,"E84"),sQuery(id+"F27.wireOp",EDGE,"E86.bottom")])],"isStart":false});
            var sketch = newSketch(context, id + "F29", { "sketchPlane" : qUnion([Q0])});
            skLineSegment(sketch, "E87.bottom", {"start": v(-41, 14.03) * mm, "end": v(-29, 14.03) * mm});
            skLineSegment(sketch, "E87.top", {"start": v(-41, -10.97) * mm, "end": v(-29, -10.97) * mm});
            skLineSegment(sketch, "E87.left", {"start": v(-41, 14.03) * mm, "end": v(-41, -10.97) * mm});
            skLineSegment(sketch, "E87.right", {"start": v(-29, 14.03) * mm, "end": v(-29, -10.97) * mm});
            skSolve(sketch);
        }
        {
            var Q0;
            Q0=qSketchRegion(id+"F29",true);
            extrude(context, id + "F30", {"entities" : qUnion([Q0]), "operationType" : NewBodyOperationType.ADD, "depth" : 3 * mm, "offsetDistance" : 25 * mm});
        }
        {
            var Q0;
            Q0=makeQuery(id+"F28.opExtrude","CAP_EDGE",EDGE,{"disambiguationData":[OSD([sQuery(id+"F27.wireOp",EDGE,"E86.bottom")])],"isStart":false});
            var Q1;
            Q1=makeQuery(id+"F28.opExtrude","CAP_EDGE",EDGE,{"disambiguationData":[OSD([sQuery(id+"F27.wireOp",EDGE,"E86.top")])],"isStart":false});
            var Q2;
            Q2=makeQuery(id+"F30.opExtrude","CAP_EDGE",EDGE,{"disambiguationData":[OSD([sQuery(id+"F29.wireOp",EDGE,"E87.top")])],"isStart":false});
            var Q3;
            Q3=makeQuery(id+"F30.opExtrude","CAP_EDGE",EDGE,{"disambiguationData":[OSD([sQuery(id+"F29.wireOp",EDGE,"E87.bottom")])],"isStart":false});
            fillet(context, id + "F31", {"entities" : qUnion([Q0, Q1, Q2, Q3]), "radius" : 2 * mm, "tangentPropagation" : true, "allowEdgeOverflow" : false});
        }
        {
            var Q0;
            Q0=makeQuery(id+"F26.opExtrude","CAP_FACE",FACE,{"disambiguationData":[OSD([sQuery(id+"F25.wireOp",EDGE,"E62.bottom"),sQuery(id+"F25.wireOp",EDGE,"E62.top"),sQuery(id+"F25.wireOp",EDGE,"E62.left"),sQuery(id+"F25.wireOp",EDGE,"E62.right"),sQuery(id+"F25.wireOp",EDGE,"E63"),sQuery(id+"F25.wireOp",EDGE,"E64"),sQuery(id+"F25.wireOp",EDGE,"E67"),sQuery(id+"F25.wireOp",EDGE,"E68"),sQuery(id+"F25.wireOp",EDGE,"E69.MirrorC"),sQuery(id+"F25.wireOp",EDGE,"E70.MirrorC"),sQuery(id+"F25.wireOp",EDGE,"E71"),sQuery(id+"F25.wireOp",EDGE,"E72.MirrorCS"),sQuery(id+"F25.wireOp",EDGE,"E73.MirrorCS"),sQuery(id+"F25.wireOp",EDGE,"E74.MirrorCS"),sQuery(id+"F25.wireOp",EDGE,"E79"),sQuery(id+"F25.wireOp",EDGE,"E80.MirrorC")])],"isStart":false});
            var sketch = newSketch(context, id + "F32", { "sketchPlane" : qUnion([Q0])});
            skLineSegment(sketch, "E88.bottom", {"start": v(-6, -51.05) * mm, "end": v(6, -51.05) * mm});
            skLineSegment(sketch, "E88.top", {"start": v(-6, -44.05) * mm, "end": v(6, -44.05) * mm});
            skLineSegment(sketch, "E88.left", {"start": v(-6, -51.05) * mm, "end": v(-6, -44.05) * mm});
            skLineSegment(sketch, "E88.right", {"start": v(6, -51.05) * mm, "end": v(6, -44.05) * mm});
            skSolve(sketch);
        }
        {
            var Q0;
            Q0=qSketchRegion(id+"F32",true);
            extrude(context, id + "F33", {"entities" : qUnion([Q0]), "operationType" : NewBodyOperationType.ADD, "depth" : 27 * mm, "offsetDistance" : 25 * mm});
        }
        {
            var Q0;
            Q0=makeQuery(id+"F33.opExtrude","CAP_EDGE",EDGE,{"disambiguationData":[OSD([sQuery(id+"F32.wireOp",EDGE,"E88.top")])],"isStart":false});
            var Q1;
            Q1=makeQuery(id+"F33.opExtrude","CAP_EDGE",EDGE,{"disambiguationData":[OSD([sQuery(id+"F32.wireOp",EDGE,"E88.bottom")])],"isStart":false});
            fillet(context, id + "F34", {"entities" : qUnion([Q0, Q1]), "radius" : 3.5 * mm, "tangentPropagation" : true, "allowEdgeOverflow" : false});
        }
    });
